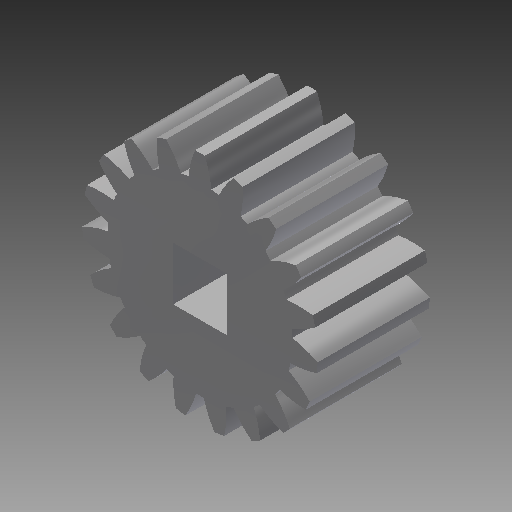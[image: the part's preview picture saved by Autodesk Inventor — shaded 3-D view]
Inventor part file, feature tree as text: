
AUTODESK INVENTOR PART (.ipt)
format: ipt  version: 2017 (Build 210142000, 142)  size: 230,400 bytes
history: native  units: mm (DEFAULTED — no unit token found)
features: plane x3, other x3, sketch x3, extrude x2
ambient origin geometry x8: Origin, YZ Plane, XZ Plane, XY Plane, X Axis, Y Axis, Z Axis, Center Point
bodies: Solid1 (feature_tree)
feature tree (11):
  extrude  "Extrusion1"  Depth=20.0mm TaperAngle=0.0deg
  plane  "Work Plane2"
  plane  "Work Plane8"
  plane  "Work Plane9"
  other  "Spur Gear"
  extrude  "Extrusion2"  Depth=10.0mm TaperAngle=0.0deg
  sketch  "Sketch1"  dims[d0=42.0mm d1=20.0mm d2=0.0mm]
  sketch  "Sketch2"  dims[d3=38.0mm d4=10.0mm d5=0.0mm]
  other  "Srf1"
  sketch  "Sketch3"  dims[d16=80.0mm d17=0.0mm d34=1.65347mm d39=0.0mm d41=0.0mm d43=80.0mm d46=80.0mm d47=0.0mm d48=0.0mm d49=9.525mm d50=10.0mm d51=0.0mm]
  other  "Pitch Diameter"
